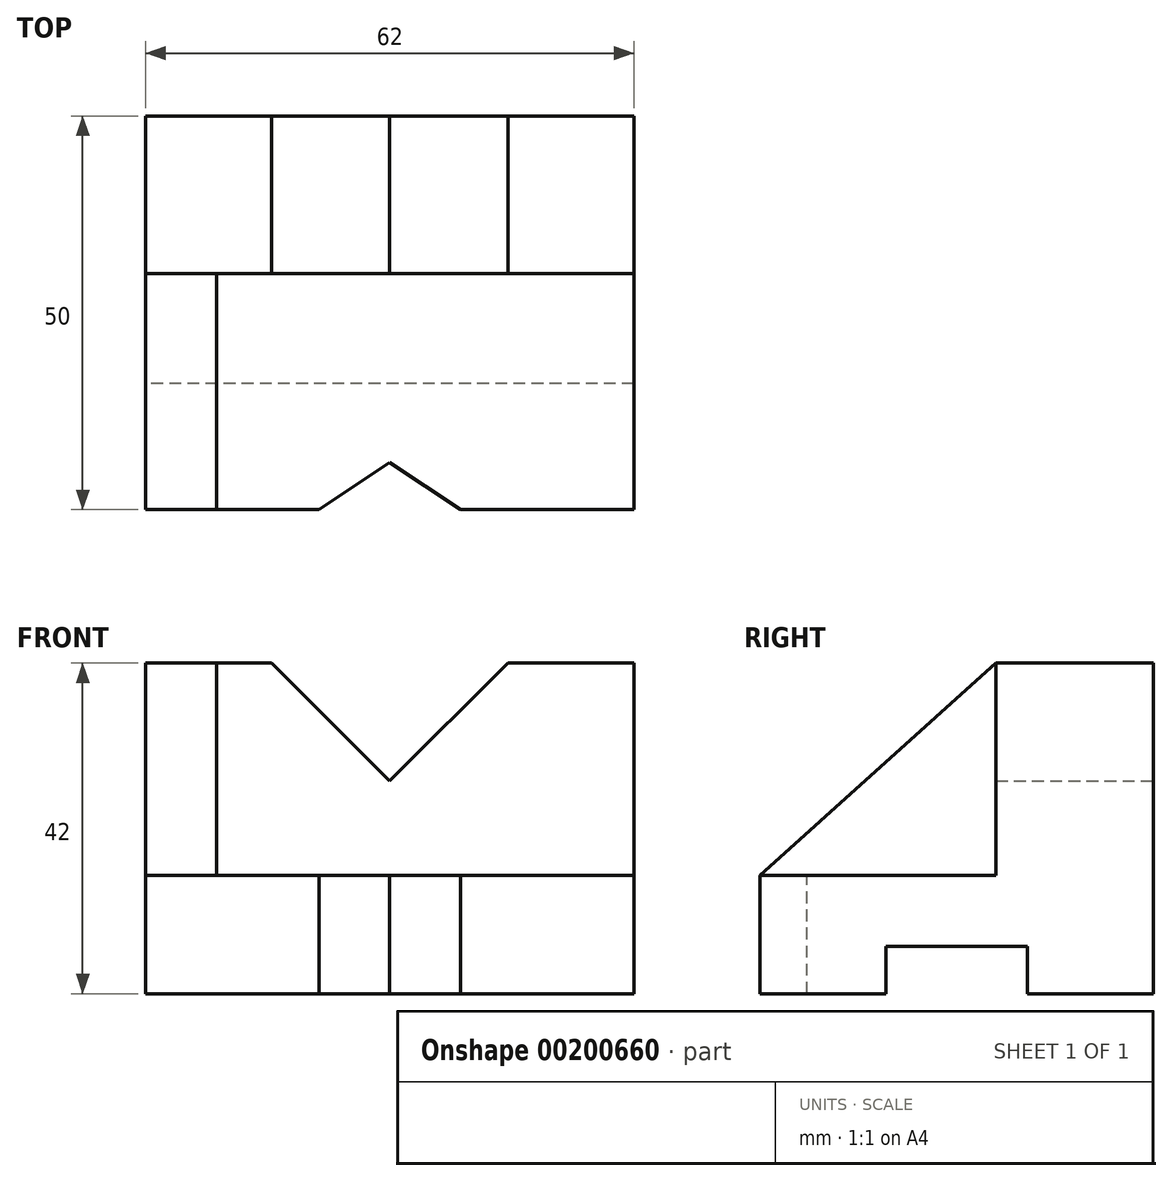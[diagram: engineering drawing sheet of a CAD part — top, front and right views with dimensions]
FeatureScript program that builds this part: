
annotation { "Feature Type Name" : "Feature", "Feature Type Description" : "" }
export const myFeature = defineFeature(function(context is Context, id is Id, definition is map)
    precondition{}
    {
        {
            var Q0;
            Q0=qCreatedBy(makeId("Front.planeOp"),FACE);
            var sketch = newSketch(context, id + "F0", { "sketchPlane" : qUnion([Q0])});
            skLineSegment(sketch, "E0", {"start": v(-31, 0) * mm, "end": v(31, 0) * mm});
            skLineSegment(sketch, "E1", {"start": v(-31, 0) * mm, "end": v(-31, 15) * mm});
            skLineSegment(sketch, "E2", {"start": v(-31, 15) * mm, "end": v(31, 15) * mm});
            skLineSegment(sketch, "E3", {"start": v(31, 15) * mm, "end": v(31, 0) * mm});
            skSolve(sketch);
        }
        {
            var Q0;
            Q0 = qSketchRegion(id + "F0", true);
            extrude(context, id + "F1", {"entities" : qUnion([Q0]), "depth" : 50 * mm});
        }
        {
            var Q0;
            Q0=makeQuery(id+"F1.opExtrude","CAP_FACE",FACE,{"disambiguationData":[OSD([sQuery(id+"F0.wireOp",EDGE,"E0"),sQuery(id+"F0.wireOp",EDGE,"E1"),sQuery(id+"F0.wireOp",EDGE,"E2"),sQuery(id+"F0.wireOp",EDGE,"E3")])],"isStart":true});
            var sketch = newSketch(context, id + "F2", { "sketchPlane" : qUnion([Q0])});
            skLineSegment(sketch, "E4.0.0", {"start": v(31, 0) * mm, "end": v(31, 15) * mm});
            skLineSegment(sketch, "E4.0.1", {"start": v(31, 15) * mm, "end": v(-31, 15) * mm});
            skLineSegment(sketch, "E4.0.2", {"start": v(-31, 15) * mm, "end": v(-31, 0) * mm});
            skLineSegment(sketch, "E4.0.3", {"start": v(-31, 0) * mm, "end": v(31, 0) * mm});
            skLineSegment(sketch, "E5", {"start": v(-31, 15) * mm, "end": v(-31, 42) * mm});
            skLineSegment(sketch, "E6", {"start": v(-31, 42) * mm, "end": v(-15, 42) * mm});
            skLineSegment(sketch, "E7", {"start": v(-15, 42) * mm, "end": v(0, 27) * mm});
            skLineSegment(sketch, "E8", {"start": v(0, 27) * mm, "end": v(15, 42) * mm});
            skLineSegment(sketch, "E9", {"start": v(15, 42) * mm, "end": v(31, 42) * mm});
            skLineSegment(sketch, "E10", {"start": v(31, 42) * mm, "end": v(31, 15) * mm});
            skSolve(sketch);
        }
        {
            var Q0;
            Q0=makeQuery(id+"F2.imprint","IMPRINT",FACE,{"disambiguationData":[TD([[makeQuery(id+"F2.imprint","IMPRINT",EDGE,{"derivedFrom":sQuery(id+"F2.wireOp",EDGE,"E4.0.1")}),-1.0]])]});
            extrude(context, id + "F3", {"entities" : qUnion([Q0]), "operationType" : NewBodyOperationType.ADD, "oppositeDirection" : true, "depth" : 20 * mm});
        }
        {
            var Q0;
            Q0=makeQuery(id+"F3.boolean.opBoolean","MERGE",FACE,{"derivedFrom":[makeQuery(id+"F1.opExtrude","SWEPT_FACE",FACE,{"disambiguationData":[OSD([sQuery(id+"F0.wireOp",EDGE,"E1")])]}),makeQuery(id+"F3.opExtrude","SWEPT_FACE",FACE,{"disambiguationData":[OSD([sQuery(id+"F2.wireOp",EDGE,"E10")])]})]});
            var sketch = newSketch(context, id + "F4", { "sketchPlane" : qUnion([Q0])});
            skSolve(sketch);
        }
        {
            var Q0;
            {var subQ1=sQuery(id+"F0.wireOp",EDGE,"E1");Q0=makeQuery(id+"F4.imprint","IMPRINT",FACE,{"disambiguationData":[TD([[makeQuery(id+"F4.imprint","IMPRINT",EDGE,{"derivedFrom":makeQuery(id+"F1.opExtrude","CAP_EDGE",EDGE,{"disambiguationData":[OSD([subQ1])],"isStart":false})}),1.0]])]});}
            var sketch = newSketch(context, id + "F5", { "sketchPlane" : qUnion([Q0])});
            skLineSegment(sketch, "E11.0", {"start": v(20, 42) * mm, "end": v(20, 15) * mm});
            skLineSegment(sketch, "E12.0", {"start": v(50, 15) * mm, "end": v(20, 15) * mm});
            skLineSegment(sketch, "E13.0", {"start": v(20, 42) * mm, "end": v(0, 42) * mm});
            skLineSegment(sketch, "E14.0", {"start": v(50, 0) * mm, "end": v(0, 0) * mm});
            skLineSegment(sketch, "E15", {"start": v(20, 42) * mm, "end": v(50, 15) * mm});
            skLineSegment(sketch, "E16", {"start": v(16, 0) * mm, "end": v(16, 6) * mm});
            skLineSegment(sketch, "E17", {"start": v(16, 6) * mm, "end": v(34, 6) * mm});
            skLineSegment(sketch, "E18", {"start": v(34, 6) * mm, "end": v(34, 0) * mm});
            skLineSegment(sketch, "E19", {"start": v(25, 0) * mm, "end": v(25, -2.1) * mm});
            skPoint(sketch, "E19.endSnap0", {"position": v(25, 0) * mm});
            skSolve(sketch);
        }
        {
            var Q0;
            {var subQ1=sQuery(id+"F0.wireOp",EDGE,"E1");Q0=makeQuery(id+"F4.imprint","IMPRINT",FACE,{"disambiguationData":[TD([[makeQuery(id+"F4.imprint","IMPRINT",EDGE,{"derivedFrom":makeQuery(id+"F1.opExtrude","CAP_EDGE",EDGE,{"disambiguationData":[OSD([subQ1])],"isStart":false})}),1.0]])]});}
            var sketch = newSketch(context, id + "F6", { "sketchPlane" : qUnion([Q0])});
            skLineSegment(sketch, "E20.0", {"start": v(20, 42) * mm, "end": v(0, 42) * mm});
            skLineSegment(sketch, "E21.0", {"start": v(50, 15) * mm, "end": v(20, 15) * mm});
            skLineSegment(sketch, "E22", {"start": v(20, 42) * mm, "end": v(50, 15) * mm});
            skPoint(sketch, "E23.0", {"position": v(20, 28.5) * mm});
            skSolve(sketch);
        }
        {
            var Q0;
            {var subQ0=sQuery(id+"F5.wireOp",EDGE,"E16");Q0=makeQuery(id+"F5.imprint","IMPRINT",FACE,{"disambiguationData":[TD([[makeQuery(id+"F5.imprint","IMPRINT",EDGE,{"derivedFrom":subQ0}),-1.0]])]});}
            extrude(context, id + "F7", {"entities" : qUnion([Q0]), "operationType" : NewBodyOperationType.REMOVE, "oppositeDirection" : true, "depth" : 62 * mm});
        }
        {
            var Q0;
            Q0 = qSketchRegion(id + "F6", true);
            var Q1;
            Q1=makeQuery(id+"F6.imprint","IMPRINT",FACE,{"disambiguationData":[TD([[makeQuery(id+"F6.imprint","IMPRINT",EDGE,{"derivedFrom":sQuery(id+"F6.wireOp",EDGE,"E21.0")}),-1.0]])]});
            extrude(context, id + "F8", {"entities" : qUnion([Q0, Q1]), "operationType" : NewBodyOperationType.ADD, "oppositeDirection" : true, "depth" : 9 * mm});
        }
        {
            var Q0;
            Q0=makeQuery(id+"F1.opExtrude","SWEPT_FACE",FACE,{"disambiguationData":[OSD([sQuery(id+"F0.wireOp",EDGE,"E2")])]});
            var sketch = newSketch(context, id + "F9", { "sketchPlane" : qUnion([Q0])});
            skLineSegment(sketch, "E24.0", {"start": v(-9, -50) * mm, "end": v(9, -50) * mm});
            skLineSegment(sketch, "E25", {"start": v(0, -44) * mm, "end": v(9, -50) * mm});
            skLineSegment(sketch, "E26", {"start": v(0, -44) * mm, "end": v(-9, -50) * mm});
            skPoint(sketch, "E27.orphan", {"position": v(22, -44) * mm});
            skPoint(sketch, "E28.end.orphan", {"position": v(-22, -44) * mm});
            skPoint(sketch, "E29.orphan", {"position": v(22, -50) * mm});
            skPoint(sketch, "E30.orphan", {"position": v(-22, -50) * mm});
            skSolve(sketch);
        }
        {
            var Q0;
            Q0 = qSketchRegion(id + "F9", true);
            extrude(context, id + "F10", {"entities" : qUnion([Q0]), "operationType" : NewBodyOperationType.REMOVE, "oppositeDirection" : true, "depth" : 25 * mm});
        }
    });
